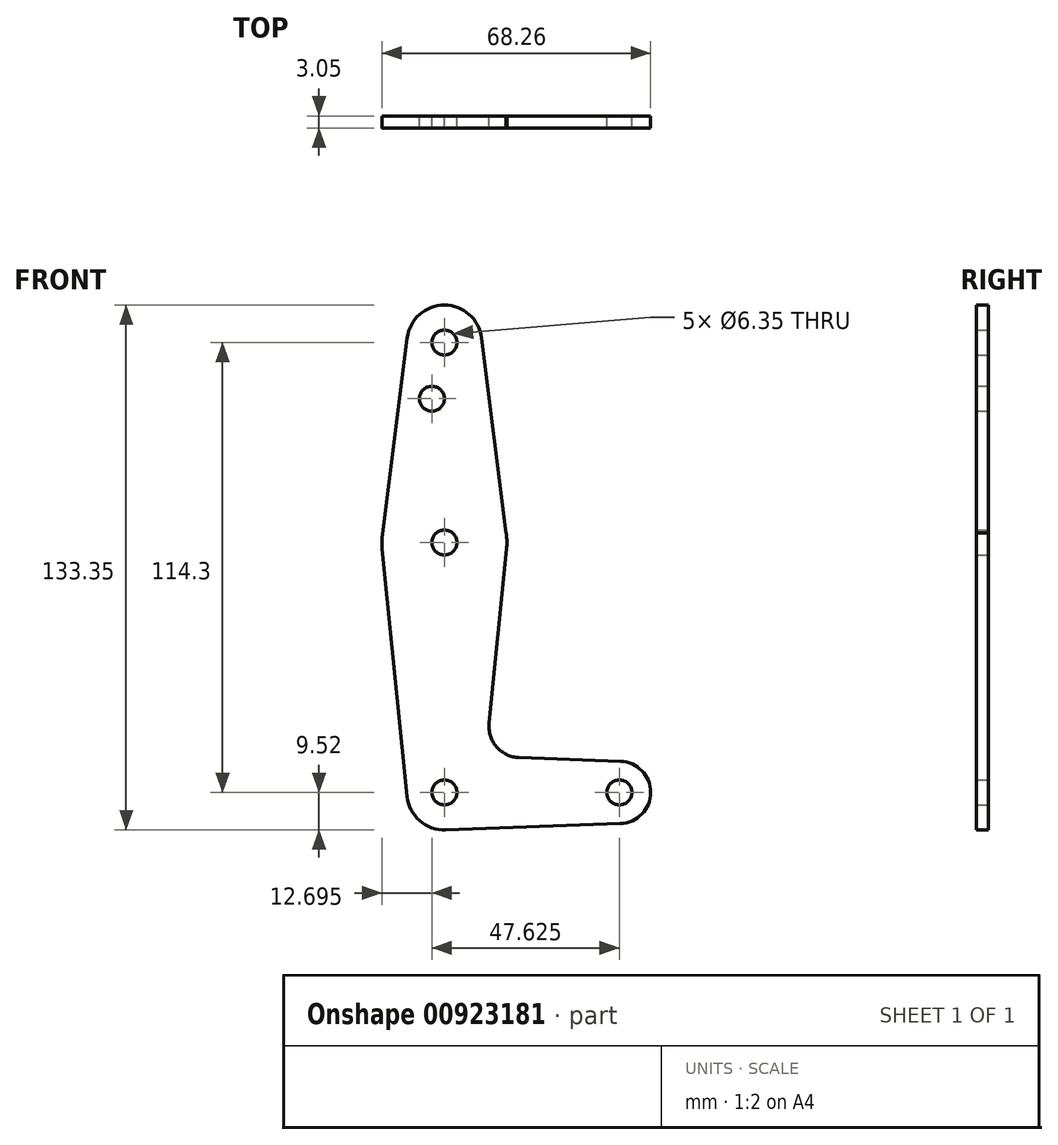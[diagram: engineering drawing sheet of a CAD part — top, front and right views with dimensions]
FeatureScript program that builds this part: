
annotation { "Feature Type Name" : "Feature", "Feature Type Description" : "" }
export const myFeature = defineFeature(function(context is Context, id is Id, definition is map)
    precondition{}
    {
        {
            var Q0;
            Q0=qCreatedBy(makeId("Front.planeOp"),FACE);
            var sketch = newSketch(context, id + "F0", { "sketchPlane" : qUnion([Q0])});
            skLineSegment(sketch, "E0", {"start": v(44.45, 0) * mm, "end": v(0, 0) * mm, "construction": true});
            skLineSegment(sketch, "E1", {"start": v(0, 0) * mm, "end": v(0, 114.3) * mm, "construction": true});
            skCircle(sketch, "E2", {"center": v(44.45, 0) * mm, "radius": 7.94 * mm});
            skCircle(sketch, "E3", {"center": v(0, 0) * mm, "radius": 9.53 * mm});
            skCircle(sketch, "E4", {"center": v(0, 63.5) * mm, "radius": 15.88 * mm});
            skCircle(sketch, "E5", {"center": v(0, 114.3) * mm, "radius": 9.53 * mm});
            skLineSegment(sketch, "E6", {"start": v(-9.45, 115.5) * mm, "end": v(-15.75, 65.48) * mm});
            skLineSegment(sketch, "E7", {"start": v(-15.8, 61.91) * mm, "end": v(-9.48, -0.95) * mm});
            skLineSegment(sketch, "E8", {"start": v(0.34, -9.52) * mm, "end": v(44.73, -7.93) * mm});
            skLineSegment(sketch, "E9", {"start": v(18.97, 8.85) * mm, "end": v(44.73, 7.93) * mm});
            skLineSegment(sketch, "E10", {"start": v(11.34, 17.6) * mm, "end": v(15.8, 61.91) * mm});
            skLineSegment(sketch, "E11", {"start": v(15.68, 65.96) * mm, "end": v(9.45, 115.49) * mm});
            skCircle(sketch, "E12", {"center": v(0, 114.3) * mm, "radius": 3.18 * mm});
            skCircle(sketch, "E13", {"center": v(0, 63.5) * mm, "radius": 3.18 * mm});
            skCircle(sketch, "E14", {"center": v(0, 0) * mm, "radius": 3.18 * mm});
            skCircle(sketch, "E15", {"center": v(44.45, 0) * mm, "radius": 3.18 * mm});
            skCircle(sketch, "E16", {"center": v(-3.18, 100.03) * mm, "radius": 3.18 * mm});
            skArc(sketch, "E17.filletArc", {"start": v(11.34, 17.6) * mm, "mid": v(13.26, 11.57) * mm, "end": v(18.97, 8.85) * mm});
            skSolve(sketch);
        }
        {
            var Q0;
            Q0=makeQuery(id+"F0.imprint","IMPRINT",FACE,{"disambiguationData":[TD([[makeQuery(id+"F0.imprint","IMPRINT",EDGE,{"derivedFrom":sQuery(id+"F0.wireOp",EDGE,"E12")}),-1.0]])]});
            var Q1;
            {var subQ1=sQuery(id+"F0.wireOp",EDGE,"E6");Q1=makeQuery(id+"F0.imprint","IMPRINT",FACE,{"disambiguationData":[TD([[makeQuery(id+"F0.imprint","IMPRINT",EDGE,{"derivedFrom":subQ1}),1.0]])]});}
            var Q2;
            Q2=makeQuery(id+"F0.imprint","IMPRINT",FACE,{"disambiguationData":[TD([[makeQuery(id+"F0.imprint","IMPRINT",EDGE,{"derivedFrom":sQuery(id+"F0.wireOp",EDGE,"E13")}),-1.0]])]});
            var Q3;
            {var subQ0=sQuery(id+"F0.wireOp",EDGE,"E7");Q3=makeQuery(id+"F0.imprint","IMPRINT",FACE,{"disambiguationData":[TD([[makeQuery(id+"F0.imprint","IMPRINT",EDGE,{"derivedFrom":subQ0}),1.0]])]});}
            var Q4;
            Q4=makeQuery(id+"F0.imprint","IMPRINT",FACE,{"disambiguationData":[TD([[makeQuery(id+"F0.imprint","IMPRINT",EDGE,{"derivedFrom":sQuery(id+"F0.wireOp",EDGE,"E14")}),-1.0]])]});
            var Q5;
            Q5=makeQuery(id+"F0.imprint","IMPRINT",FACE,{"disambiguationData":[TD([[makeQuery(id+"F0.imprint","IMPRINT",EDGE,{"derivedFrom":sQuery(id+"F0.wireOp",EDGE,"E15")}),-1.0]])]});
            extrude(context, id + "F1", {"entities" : qUnion([Q0, Q1, Q2, Q3, Q4, Q5]), "depth" : 3.05 * mm, "offsetDistance" : 25.4 * mm});
        }
    });
